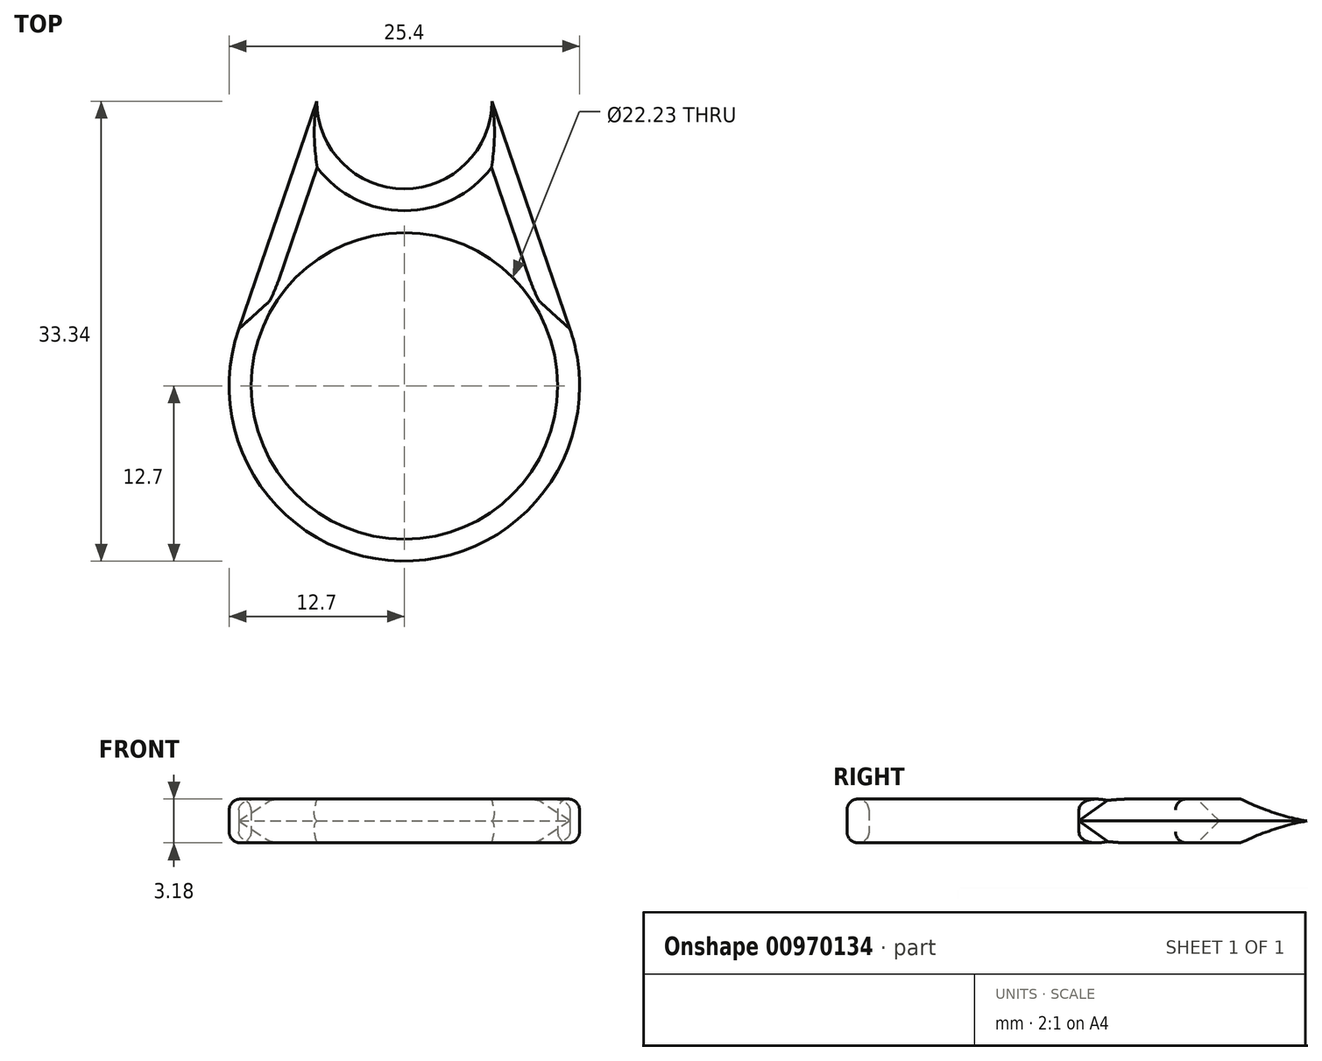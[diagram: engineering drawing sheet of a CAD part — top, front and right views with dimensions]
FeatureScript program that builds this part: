
annotation { "Feature Type Name" : "Feature", "Feature Type Description" : "" }
export const myFeature = defineFeature(function(context is Context, id is Id, definition is map)
    precondition{}
    {
        {
            var Q0;
            Q0=qCreatedBy(makeId("Top.planeOp"),FACE);
            var sketch = newSketch(context, id + "F0", { "sketchPlane" : qUnion([Q0])});
            skCircle(sketch, "E0", {"center": v(0, 0) * mm, "radius": 11.11 * mm});
            skArc(sketch, "E1", {"start": v(-12.01, 4.12) * mm, "mid": v(0, -12.7) * mm, "end": v(12.01, 4.12) * mm});
            skPoint(sketch, "E2", {"position": v(0, 20.64) * mm});
            skLineSegment(sketch, "E3", {"start": v(-12.01, 4.12) * mm, "end": v(-6.35, 20.64) * mm});
            skLineSegment(sketch, "E4", {"start": v(12.01, 4.12) * mm, "end": v(6.35, 20.64) * mm});
            skArc(sketch, "E5", {"start": v(-6.35, 20.64) * mm, "mid": v(0, 14.29) * mm, "end": v(6.35, 20.64) * mm});
            skLineSegment(sketch, "E6", {"start": v(-12.01, 4.12) * mm, "end": v(-7.45, 8.24) * mm});
            skLineSegment(sketch, "E7", {"start": v(12.01, 4.12) * mm, "end": v(7.45, 8.24) * mm});
            skSolve(sketch);
        }
        {
            var Q0;
            Q0=makeQuery(id+"F0.imprint","IMPRINT",FACE,{"disambiguationData":[TD([[makeQuery(id+"F0.imprint","IMPRINT",EDGE,{"derivedFrom":sQuery(id+"F0.wireOp",EDGE,"E3")}),-1.0]])]});
            extrude(context, id + "F1", {"entities" : qUnion([Q0]), "depth" : 3.17 * mm, "offsetDistance" : 25.4 * mm});
        }
        {
            var Q0;
            Q0=makeQuery(id+"F1.opExtrude","CAP_EDGE",EDGE,{"disambiguationData":[OSD([sQuery(id+"F0.wireOp",EDGE,"E3")])],"isStart":false});
            var Q1;
            Q1=makeQuery(id+"F1.opExtrude","CAP_EDGE",EDGE,{"disambiguationData":[OSD([sQuery(id+"F0.wireOp",EDGE,"E3")])],"isStart":true});
            var Q2;
            Q2=makeQuery(id+"F1.opExtrude","CAP_EDGE",EDGE,{"disambiguationData":[OSD([sQuery(id+"F0.wireOp",EDGE,"E5")])],"isStart":true});
            var Q3;
            Q3=makeQuery(id+"F1.opExtrude","CAP_EDGE",EDGE,{"disambiguationData":[OSD([sQuery(id+"F0.wireOp",EDGE,"E5")])],"isStart":false});
            var Q4;
            Q4=makeQuery(id+"F1.opExtrude","CAP_EDGE",EDGE,{"disambiguationData":[OSD([sQuery(id+"F0.wireOp",EDGE,"E4")])],"isStart":false});
            var Q5;
            Q5=makeQuery(id+"F1.opExtrude","CAP_EDGE",EDGE,{"disambiguationData":[OSD([sQuery(id+"F0.wireOp",EDGE,"E4")])],"isStart":true});
            chamfer(context, id + "F2", {"entities" : qUnion([Q0, Q1, Q2, Q3, Q4, Q5]), "width" : 1.59 * mm, "tangentPropagation" : true});
        }
        {
            var Q0;
            Q0=makeQuery(id+"F0.imprint","IMPRINT",FACE,{"disambiguationData":[TD([[makeQuery(id+"F0.imprint","IMPRINT",EDGE,{"derivedFrom":sQuery(id+"F0.wireOp",EDGE,"E1")}),1.0]])]});
            extrude(context, id + "F3", {"entities" : qUnion([Q0]), "operationType" : NewBodyOperationType.ADD, "depth" : 3.17 * mm, "offsetDistance" : 25.4 * mm});
        }
        {
            var Q0;
            {var subQ0=sQuery(id+"F0.wireOp",EDGE,"E0");Q0=makeQuery(id+"F3.boolean.opBoolean","MERGE",EDGE,{"derivedFrom":[makeQuery(id+"F1.opExtrude","CAP_EDGE",EDGE,{"disambiguationData":[OSD([subQ0])],"isStart":false}),makeQuery(id+"F3.opExtrude","CAP_EDGE",EDGE,{"disambiguationData":[OSD([subQ0])],"isStart":false})]});}
            var Q1;
            {var subQ0=sQuery(id+"F0.wireOp",EDGE,"E0");Q1=makeQuery(id+"F3.boolean.opBoolean","MERGE",EDGE,{"derivedFrom":[makeQuery(id+"F1.opExtrude","CAP_EDGE",EDGE,{"disambiguationData":[OSD([subQ0])],"isStart":true}),makeQuery(id+"F3.opExtrude","CAP_EDGE",EDGE,{"disambiguationData":[OSD([subQ0])],"isStart":true})]});}
            var Q2;
            Q2=makeQuery(id+"F3.opExtrude","CAP_EDGE",EDGE,{"disambiguationData":[OSD([sQuery(id+"F0.wireOp",EDGE,"E1")])],"isStart":true});
            var Q3;
            Q3=makeQuery(id+"F3.opExtrude","CAP_EDGE",EDGE,{"disambiguationData":[OSD([sQuery(id+"F0.wireOp",EDGE,"E1")])],"isStart":false});
            fillet(context, id + "F4", {"entities" : qUnion([Q0, Q1, Q2, Q3]), "radius" : 0.8 * mm, "tangentPropagation" : true, "allowEdgeOverflow" : false});
        }
    });
